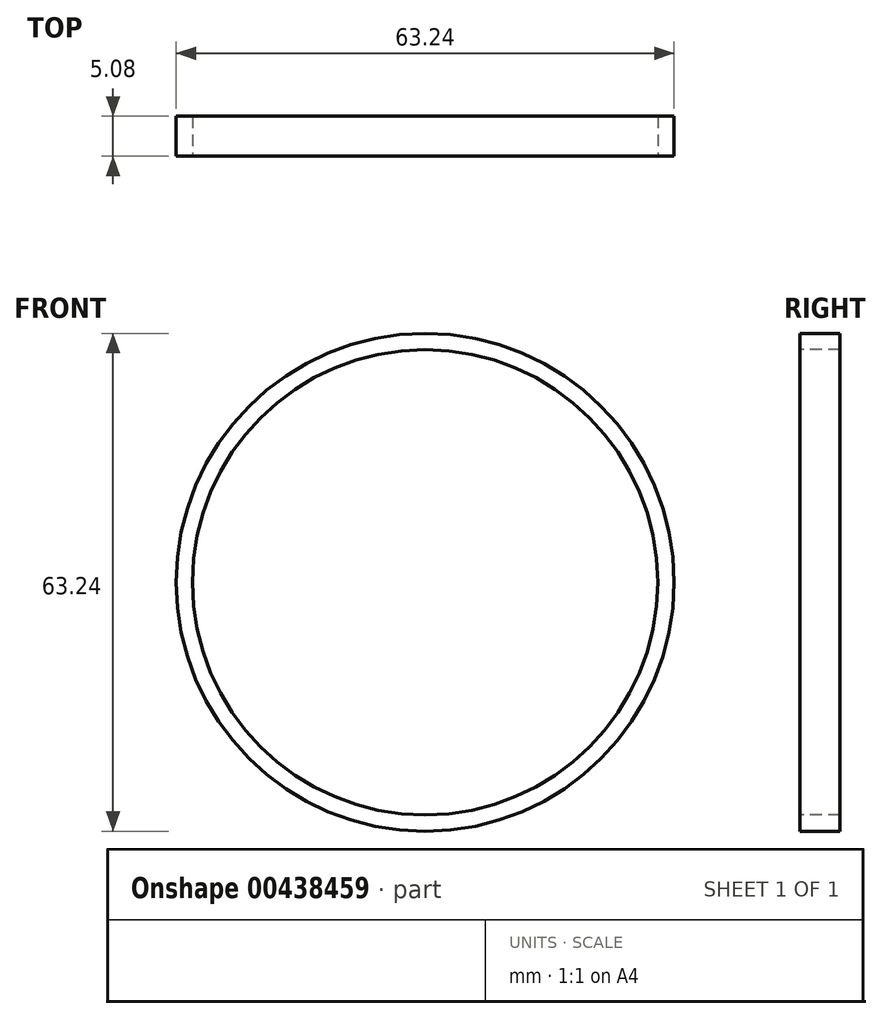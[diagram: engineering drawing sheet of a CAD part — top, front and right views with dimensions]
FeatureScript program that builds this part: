
annotation { "Feature Type Name" : "Feature", "Feature Type Description" : "" }
export const myFeature = defineFeature(function(context is Context, id is Id, definition is map)
    precondition{}
    {
        {
            var Q0;
            Q0=qCreatedBy(makeId("Front.planeOp"),FACE);
            var sketch = newSketch(context, id + "F0", { "sketchPlane" : qUnion([Q0])});
            skCircle(sketch, "E0", {"center": v(0, 0) * mm, "radius": 31.62 * mm});
            skCircle(sketch, "E1", {"center": v(0, 0) * mm, "radius": 29.55 * mm});
            skSolve(sketch);
        }
        {
            var Q0;
            Q0=sQuery(id+"F0.wireOp",EDGE,"E0");
            var Q1;
            Q1=sQuery(id+"F0.wireOp",EDGE,"E1");
            extrude(context, id + "F1", {"bodyType" : ToolBodyType.SURFACE, "surfaceEntities" : qUnion([Q0, Q1]), "depth" : 5.08 * mm});
        }
    });
